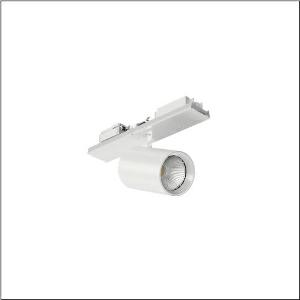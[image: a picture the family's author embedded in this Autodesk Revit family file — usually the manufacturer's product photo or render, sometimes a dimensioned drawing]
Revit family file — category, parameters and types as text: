
# Revit family: licross_r__spot_31_51sl14da45b_0bda
name_source: partatom
category: Lighting Fixtures
units: mm (PartAtom-declared; Revit-internal decimal feet)

## family parameters
Cut with Voids When Loaded = No
Host = Face
Light Source = No
Part Type = Normal
Room Calculation Point = No
Round Connector Dimension = Use Diameter
Shared = No

## types (1)
- --- (1 x LED, 5250 lm, 43.7 W, 4000K)
    Apparent Load = 44 VA
    CIE Flux Codes = 93 97 100 100 100
    Color Rendering = 90
    Color Temperature = 4000K
    Default Elevation = 1800 mm
    Description = Licross® Spot 31, directional spotlight, light control with lens, of plastic, LED rated luminous flux: 5.250lm, light colour: 940, with plug, 5-pole, mains connection: 220..240V, AC, 50/60Hz, of aluminium, traffic white (RAL 9016), length: 140mm, diameter: 90mm, protection rating (complete): IP20, insulation class (complete): insulation class I (protective earthing), certification: CE, packaging unit: 1 piece
    Height = 175 mm
    Lamp = 1 x LED
    Lamp Light Flux = 5250 lm
    Lamp Power = 43.7 W
    Lamp count = 1
    Length = 90 mm
    Luminous efficacy = 120 lm/W
    Manufacturer = Siteco
    ModVariant = No
    Model = 51SL14DA45B
    Mounting Place = Ceiling
    Mounting Type = Pendant
    Number of Poles = 1
    OnlyDefault = Yes
    Power Factor = 1
    Product Name = Licross® Spot 31
    Product group = directional spotlight
    ProductGroupID = 905
    Protection Class = Protection class I
    Protection Degree = IP 20
    RLX_Detail_Level = 1
    RLX_Emergency_Light_Flux = 0 lm
    RLX_Emergency_Type = 0
    RLX_Emergency_Type_DB = No
    RlxData = <blob elided: 14861 chars, md5=9cd1b875>
    Socket = socket
    Standby Power = 0 W
    System Light Flux = 5250 lm
    System Power = 44 W
    Type Comments = factory setting: luminous flux: 100 % | (ON | ON | ON) | 1050 mA
    Type Image = l_1245720.jpg
    URL = http://relux.com
    VarID = @adj_063591
    Voltage = 0 V
    Weight = 0.00 kg
    Width = 0 mm  [stored 0 ft]

note: [stored X ft] marks values corroborated as IEEE doubles in the binary element streams (Revit-internal decimal feet)

## geometry (parser evidence)
native form markers: Sweep x12
no freeform markers — native parametric forms only
